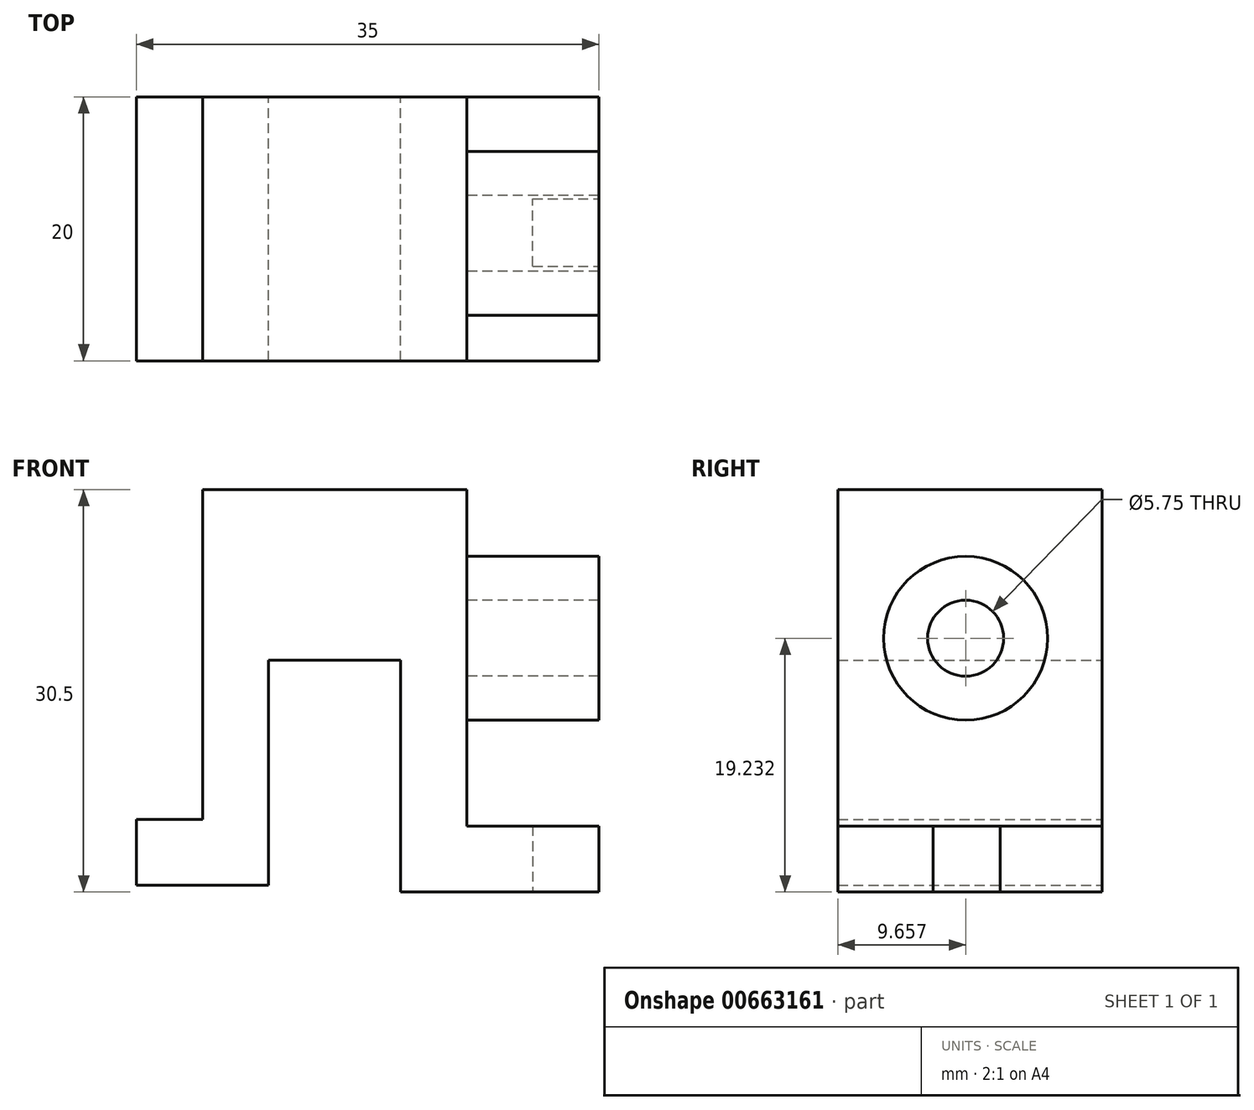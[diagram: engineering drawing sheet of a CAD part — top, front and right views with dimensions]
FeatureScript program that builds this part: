
annotation { "Feature Type Name" : "Feature", "Feature Type Description" : "" }
export const myFeature = defineFeature(function(context is Context, id is Id, definition is map)
    precondition{}
    {
        {
            var Q0;
            Q0=qCreatedBy(makeId("Front.planeOp"),FACE);
            var sketch = newSketch(context, id + "F0", { "sketchPlane" : qUnion([Q0])});
            skLineSegment(sketch, "E0", {"start": v(-24.9, -11.02) * mm, "end": v(-24.9, -6.02) * mm});
            skLineSegment(sketch, "E1", {"start": v(-24.9, -6.02) * mm, "end": v(-19.9, -6.02) * mm});
            skLineSegment(sketch, "E2", {"start": v(-19.9, -6.02) * mm, "end": v(-19.9, 18.98) * mm});
            skLineSegment(sketch, "E3", {"start": v(-19.9, 18.98) * mm, "end": v(0.1, 18.98) * mm});
            skLineSegment(sketch, "E4", {"start": v(0.1, 18.98) * mm, "end": v(0.1, -6.52) * mm});
            skLineSegment(sketch, "E5", {"start": v(0.1, -6.52) * mm, "end": v(10.1, -6.52) * mm});
            skLineSegment(sketch, "E6", {"start": v(10.1, -6.52) * mm, "end": v(10.1, -11.52) * mm});
            skLineSegment(sketch, "E7", {"start": v(10.1, -11.52) * mm, "end": v(-4.9, -11.52) * mm});
            skLineSegment(sketch, "E8", {"start": v(-4.9, -11.52) * mm, "end": v(-4.9, 6.05) * mm});
            skLineSegment(sketch, "E9", {"start": v(-4.9, 6.05) * mm, "end": v(-14.9, 6.05) * mm});
            skLineSegment(sketch, "E10", {"start": v(-14.9, 6.05) * mm, "end": v(-14.9, -11.02) * mm});
            skLineSegment(sketch, "E11", {"start": v(-14.9, -11.02) * mm, "end": v(-24.9, -11.02) * mm});
            skSolve(sketch);
        }
        {
            var Q0;
            Q0=makeQuery(id+"F0.imprint","IMPRINT",FACE,{"disambiguationData":[TD([[makeQuery(id+"F0.imprint","IMPRINT",EDGE,{"derivedFrom":sQuery(id+"F0.wireOp",EDGE,"E0")}),-1.0]])]});
            extrude(context, id + "F1", {"entities" : qUnion([Q0]), "depth" : 20 * mm, "offsetDistance" : 25 * mm});
        }
        {
            var Q0;
            Q0=makeQuery(id+"F1.opExtrude","SWEPT_FACE",FACE,{"disambiguationData":[OSD([sQuery(id+"F0.wireOp",EDGE,"E6")])]});
            var sketch = newSketch(context, id + "F2", { "sketchPlane" : qUnion([Q0])});
            skLineSegment(sketch, "E12", {"start": v(-12.82, -6.52) * mm, "end": v(-12.82, -11.52) * mm});
            skPoint(sketch, "E12.endSnap0", {"position": v(-10, -11.52) * mm});
            skLineSegment(sketch, "E13", {"start": v(-12.82, -11.52) * mm, "end": v(-7.72, -11.52) * mm});
            skLineSegment(sketch, "E14", {"start": v(-7.72, -11.52) * mm, "end": v(-7.72, -6.52) * mm});
            skLineSegment(sketch, "E15", {"start": v(-7.72, -6.52) * mm, "end": v(-12.82, -6.52) * mm});
            skSolve(sketch);
        }
        {
            var Q0;
            Q0=makeQuery(id+"F2.imprint","IMPRINT",FACE,{"disambiguationData":[TD([[makeQuery(id+"F2.imprint","IMPRINT",EDGE,{"derivedFrom":sQuery(id+"F2.wireOp",EDGE,"E12")}),1.0]])]});
            extrude(context, id + "F3", {"entities" : qUnion([Q0]), "operationType" : NewBodyOperationType.REMOVE, "oppositeDirection" : true, "depth" : 5 * mm, "offsetDistance" : 25 * mm});
        }
        {
            var Q0;
            Q0=makeQuery(id+"F1.opExtrude","SWEPT_FACE",FACE,{"disambiguationData":[OSD([sQuery(id+"F0.wireOp",EDGE,"E4")])]});
            var sketch = newSketch(context, id + "F4", { "sketchPlane" : qUnion([Q0])});
            skCircle(sketch, "E16", {"center": v(-10.34, 7.71) * mm, "radius": 6.2 * mm});
            skCircle(sketch, "E17", {"center": v(-10.34, 7.71) * mm, "radius": 2.88 * mm});
            skSolve(sketch);
        }
        {
            var Q0;
            Q0=makeQuery(id+"F4.imprint","IMPRINT",FACE,{"disambiguationData":[TD([[makeQuery(id+"F4.imprint","IMPRINT",EDGE,{"derivedFrom":sQuery(id+"F4.wireOp",EDGE,"E16")}),1.0]])]});
            extrude(context, id + "F5", {"entities" : qUnion([Q0]), "depth" : 10 * mm, "offsetDistance" : 25 * mm});
        }
    });
